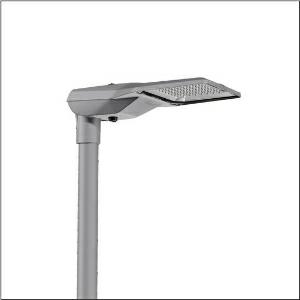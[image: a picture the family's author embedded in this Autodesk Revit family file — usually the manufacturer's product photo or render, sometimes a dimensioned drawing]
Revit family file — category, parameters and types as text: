
# Revit family: streetlight_sl_21_midi___stw1_0a_5xe3e63t08nb_c3f7
name_source: partatom
category: Lighting Fixtures
units: mm (PartAtom-declared; Revit-internal decimal feet)

## family parameters
Cut with Voids When Loaded = No
Host = Face
Light Source = No
Part Type = Normal
Room Calculation Point = No
Round Connector Dimension = Use Diameter
Shared = No

## types (1)
- --- (1 x LED, 20350 lm, 151.2 W, 2700K)
    Apparent Load = 151 VA
    CIE Flux Codes = 39 75 98 100 100
    Color Rendering = 70
    Color Temperature = 2700K
    Default Elevation = 1800 mm
    Description = Streetlight SL 21 midi, mast luminaire, primary light control with lens, of PMMA, primary optical cover: cover, of toughened safety glass, transparent, light distribution: STW1.0a, light emission: direct distribution, primary light characteristic: asymmetric, installation type: side-entry, post-top, LED, High Power LED, rated luminous flux: 20.350lm, luminous efficacy: 135lm/W, light colour: 727, colour temperature: 2700K, control gear: D4i, control: overheat protection, constant luminous flux control, time-dependent luminous flux control, flexible luminous flux parameterisation, pre-setting: logarithmic dimming characteristic, mains connection: 230..240V, AC, 50/60Hz, start of lifetime: 151W, end of service life: 157W, reduction: 70W, luminaire housing, of diecast aluminium, powder-coated, SITECO metallic grey (DB 702S), corrosivity category C5 high according to DIN EN ISO 12944, please order mast flange separately, inclination adjustable: 0°, 5°, 10°, 15°, sealing non-destructively replaceable, multi-level sealing system, length: 644mm, width: 335mm, height: 110mm, mast flange for spigot size: 42mm (side-entry): 5XC10008XM4, 60/48mm (side-entry/post-top): 5XC10108XM2, 76/60mm (side-entry/post-top): 5XC10108XM1, mounting height: 4..8m, Smart Interface below and above, protection rating (complete): IP66, insulation class (complete): insulation class II (safety insulation), certification: CE, ENEC, ENEC+, VDE, impact resistance: IK10, permissible operating ambient temperature for outdoor applications: -40..+50°C, standard-compliant lighting for roads and squares, packaging unit: 1 piece

Light Distribution: STW1.0a
    Height = 111 mm
    Lamp = 1 x LED
    Lamp Light Flux = 20350 lm
    Lamp Power = 151.2 W
    Lamp count = 1
    Length = 644 mm
    Luminous efficacy = 135 lm/W
    Manufacturer = Siteco
    ModVariant = No
    Model = 5XE3E63T08NB
    Number of Poles = 1
    OnlyDefault = Yes
    Power Factor = 1
    Product Name = Streetlight SL 21 midi | STW1.0a
    Product group = mast luminaire | pylon top
    ProductGroupID = 6100
    Protection Class = Protection class II
    Protection Degree = IP 66
    RLX_Detail_Level = 1
    RLX_Emergency_Light_Flux = 0 lm
    RLX_Emergency_Type = 0
    RLX_Emergency_Type_DB = No
    RlxData = <blob elided: 27197 chars, md5=7a7052da>
    Socket = socket
    Standby Power = 0 W
    System Light Flux = 20350 lm
    System Power = 151 W
    Type Comments = factory setting: luminous flux: 100 % | dim-lin: 254 | 802 mA
    Type Image = l_1004304.jpg
    URL = http://relux.com
    VarID = @adj_168973
    Voltage = 0 V
    Weight = 0.00 kg
    Width = 336 mm

## geometry (parser evidence)
native form markers: Blend x4, Sweep x11
no freeform markers — native parametric forms only
